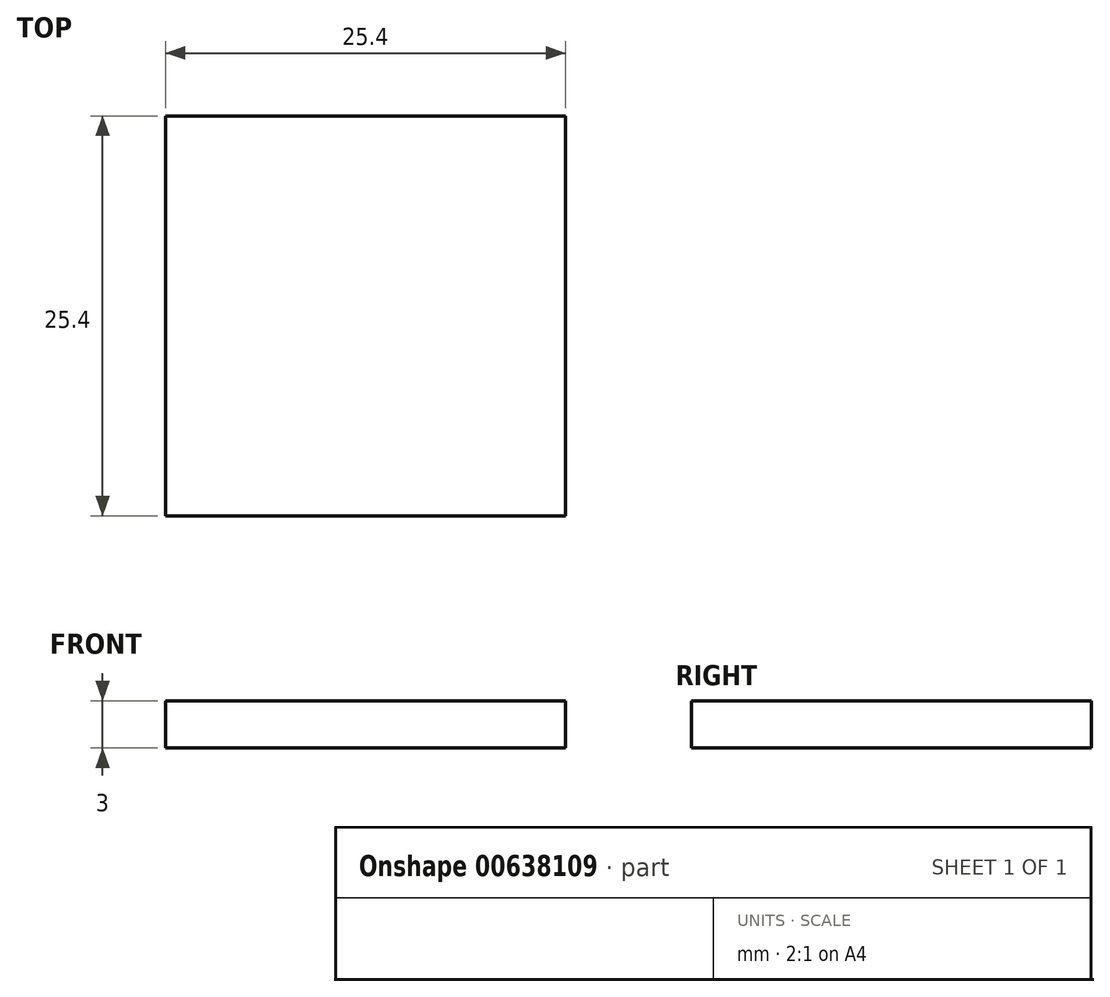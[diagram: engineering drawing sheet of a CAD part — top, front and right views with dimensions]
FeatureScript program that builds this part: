
annotation { "Feature Type Name" : "Feature", "Feature Type Description" : "" }
export const myFeature = defineFeature(function(context is Context, id is Id, definition is map)
    precondition{}
    {
        {
            var Q0;
            Q0=qCreatedBy(makeId("Top.planeOp"),FACE);
            var sketch = newSketch(context, id + "F0", { "sketchPlane" : qUnion([Q0])});
            skLineSegment(sketch, "E0.bottom", {"start": v(0, 0) * mm, "end": v(25.4, 0) * mm});
            skLineSegment(sketch, "E0.top", {"start": v(0, -25.4) * mm, "end": v(25.4, -25.4) * mm});
            skLineSegment(sketch, "E0.left", {"start": v(0, 0) * mm, "end": v(0, -25.4) * mm});
            skLineSegment(sketch, "E0.right", {"start": v(25.4, 0) * mm, "end": v(25.4, -25.4) * mm});
            skSolve(sketch);
        }
        {
            var Q0;
            Q0=makeQuery(id+"F0.imprint","IMPRINT",FACE,{"disambiguationData":[TD([[makeQuery(id+"F0.imprint","IMPRINT",EDGE,{"derivedFrom":sQuery(id+"F0.wireOp",EDGE,"E0.bottom")}),-1.0]])]});
            extrude(context, id + "F1", {"entities" : qUnion([Q0]), "depth" : 3 * mm, "offsetDistance" : 25.4 * mm});
        }
    });
